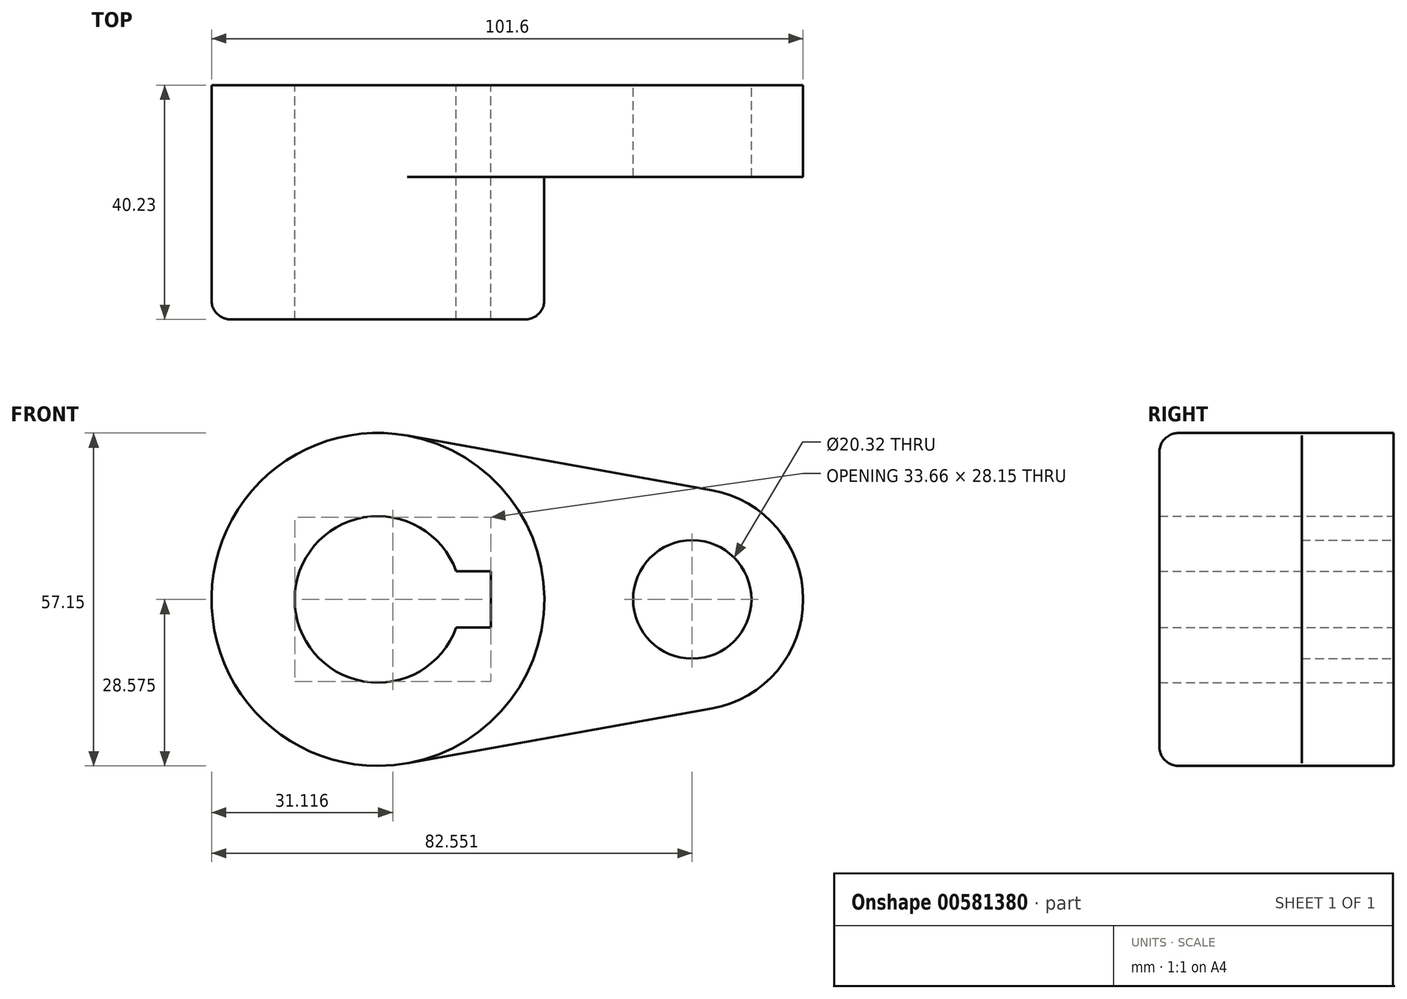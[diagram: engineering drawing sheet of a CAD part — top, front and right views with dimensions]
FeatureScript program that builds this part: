
annotation { "Feature Type Name" : "Feature", "Feature Type Description" : "" }
export const myFeature = defineFeature(function(context is Context, id is Id, definition is map)
    precondition{}
    {
        {
            var Q0;
            Q0=qCreatedBy(makeId("Front.planeOp"),FACE);
            var sketch = newSketch(context, id + "F0", { "sketchPlane" : qUnion([Q0])});
            skCircle(sketch, "E0", {"center": v(-24.25, -4.37) * mm, "radius": 28.58 * mm});
            skCircle(sketch, "E1", {"center": v(-24.25, -4.37) * mm, "radius": 14.29 * mm});
            skLineSegment(sketch, "E2", {"start": v(-24.25, -4.37) * mm, "end": v(29.72, -4.37) * mm, "construction": true});
            skLineSegment(sketch, "E3", {"start": v(-37.7, 0.46) * mm, "end": v(-4.89, 0.46) * mm, "construction": true});
            skLineSegment(sketch, "E4", {"start": v(-4.89, 0.46) * mm, "end": v(-4.89, -9.2) * mm, "construction": true});
            skLineSegment(sketch, "E5", {"start": v(-4.89, -9.2) * mm, "end": v(-37.7, -9.2) * mm, "construction": true});
            skLineSegment(sketch, "E6", {"start": v(-37.7, -9.2) * mm, "end": v(-37.7, 0.46) * mm, "construction": true});
            skLineSegment(sketch, "E7.bottom", {"start": v(-37.7, 0.46) * mm, "end": v(-4.89, 0.46) * mm});
            skLineSegment(sketch, "E7.top", {"start": v(-37.7, -9.2) * mm, "end": v(-4.89, -9.2) * mm});
            skLineSegment(sketch, "E7.left", {"start": v(-37.7, 0.46) * mm, "end": v(-37.7, -9.2) * mm});
            skLineSegment(sketch, "E7.right", {"start": v(-4.89, 0.46) * mm, "end": v(-4.89, -9.2) * mm});
            skLineSegment(sketch, "E8", {"start": v(-24.25, -4.37) * mm, "end": v(-24.25, 62.22) * mm, "construction": true});
            skLineSegment(sketch, "E9", {"start": v(-24.25, 62.22) * mm, "end": v(-24.25, -56.69) * mm, "construction": true});
            skCircle(sketch, "E10", {"center": v(29.72, -4.37) * mm, "radius": 19.05 * mm});
            skLineSegment(sketch, "E11", {"start": v(-19.21, 23.76) * mm, "end": v(33.08, 14.39) * mm});
            skLineSegment(sketch, "E12", {"start": v(-19.21, -32.5) * mm, "end": v(33.08, -23.12) * mm});
            skCircle(sketch, "E13", {"center": v(29.72, -4.37) * mm, "radius": 10.16 * mm});
            skSolve(sketch);
        }
        {
            var Q0;
            {var subQ10=sQuery(id+"F0.wireOp",EDGE,"E7.right");Q0=makeQuery(id+"F0.imprint","IMPRINT",FACE,{"disambiguationData":[TD([[makeQuery(id+"F0.imprint","IMPRINT",EDGE,{"derivedFrom":subQ10}),1.0]])]});}
            extrude(context, id + "F1", {"entities" : qUnion([Q0]), "depth" : 40.23 * mm, "offsetDistance" : 25.4 * mm});
        }
        {
            var Q0;
            {var subQ0=sQuery(id+"F0.wireOp",EDGE,"E11");Q0=makeQuery(id+"F0.imprint","IMPRINT",FACE,{"disambiguationData":[TD([[makeQuery(id+"F0.imprint","IMPRINT",EDGE,{"derivedFrom":subQ0}),-1.0]])]});}
            var Q1;
            Q1=makeQuery(id+"F0.imprint","IMPRINT",FACE,{"disambiguationData":[TD([[makeQuery(id+"F0.imprint","IMPRINT",EDGE,{"derivedFrom":sQuery(id+"F0.wireOp",EDGE,"E13")}),-1.0]])]});
            extrude(context, id + "F2", {"entities" : qUnion([Q0, Q1]), "operationType" : NewBodyOperationType.ADD, "depth" : 15.77 * mm, "offsetDistance" : 25.4 * mm});
        }
        {
            var Q0;
            Q0=makeQuery(id+"F1.opExtrude","CAP_EDGE",EDGE,{"disambiguationData":[OSD([sQuery(id+"F0.wireOp",EDGE,"E0")])],"isStart":false});
            fillet(context, id + "F3", {"entities" : qUnion([Q0]), "radius" : 3.3 * mm, "tangentPropagation" : true, "allowEdgeOverflow" : false});
        }
    });
